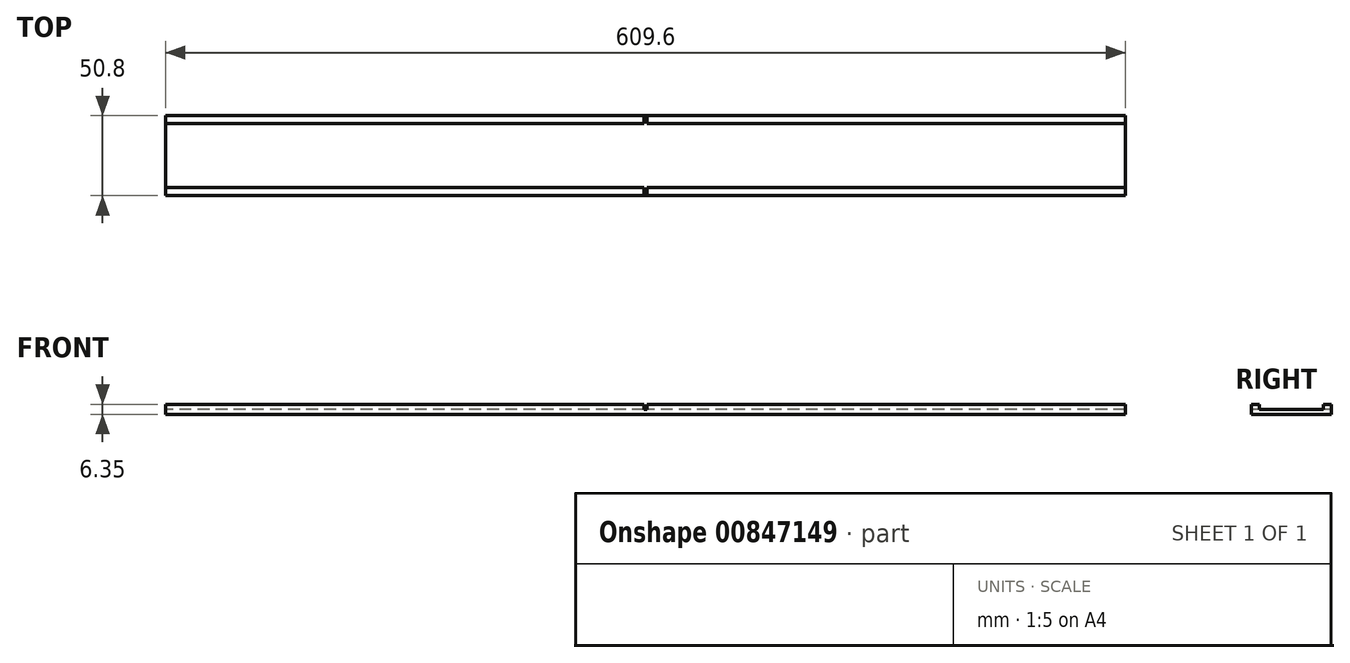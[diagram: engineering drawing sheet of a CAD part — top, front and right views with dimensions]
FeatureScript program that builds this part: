
annotation { "Feature Type Name" : "Feature", "Feature Type Description" : "" }
export const myFeature = defineFeature(function(context is Context, id is Id, definition is map)
    precondition{}
    {
        {
            var Q0;
            Q0=qCreatedBy(makeId("Top.planeOp"),FACE);
            var sketch = newSketch(context, id + "F0", { "sketchPlane" : qUnion([Q0])});
            skLineSegment(sketch, "E0.bottom", {"start": v(304.8, -25.4) * mm, "end": v(-304.8, -25.4) * mm});
            skLineSegment(sketch, "E0.top", {"start": v(304.8, 25.4) * mm, "end": v(-304.8, 25.4) * mm});
            skLineSegment(sketch, "E0.left", {"start": v(304.8, -25.4) * mm, "end": v(304.8, 25.4) * mm});
            skLineSegment(sketch, "E0.right", {"start": v(-304.8, -25.4) * mm, "end": v(-304.8, 25.4) * mm});
            skPoint(sketch, "E0.middle", {"position": v(0, 0) * mm});
            skSolve(sketch);
        }
        {
            var Q0;
            Q0 = qSketchRegion(id + "F0", true);
            extrude(context, id + "F1", {"entities" : qUnion([Q0]), "depth" : 6.35 * mm, "offsetDistance" : 25.4 * mm});
        }
        {
            var Q0;
            Q0=makeQuery(id+"F1.opExtrude","CAP_FACE",FACE,{"disambiguationData":[OSD([sQuery(id+"F0.wireOp",EDGE,"E0.bottom"),sQuery(id+"F0.wireOp",EDGE,"E0.top"),sQuery(id+"F0.wireOp",EDGE,"E0.left"),sQuery(id+"F0.wireOp",EDGE,"E0.right")])],"isStart":false});
            var sketch = newSketch(context, id + "F2", { "sketchPlane" : qUnion([Q0])});
            skLineSegment(sketch, "E1.bottom", {"start": v(304.8, -20.32) * mm, "end": v(-304.8, -20.32) * mm});
            skLineSegment(sketch, "E1.top", {"start": v(304.8, 20.32) * mm, "end": v(-304.8, 20.32) * mm});
            skLineSegment(sketch, "E1.left", {"start": v(304.8, -20.32) * mm, "end": v(304.8, 20.32) * mm});
            skLineSegment(sketch, "E1.right", {"start": v(-304.8, -20.32) * mm, "end": v(-304.8, 20.32) * mm});
            skPoint(sketch, "E1.middle", {"position": v(0, 0) * mm});
            skSolve(sketch);
        }
        {
            var Q0;
            Q0 = qSketchRegion(id + "F2", true);
            extrude(context, id + "F3", {"entities" : qUnion([Q0]), "operationType" : NewBodyOperationType.REMOVE, "oppositeDirection" : true, "depth" : 3.17 * mm, "offsetDistance" : 25.4 * mm});
        }
        {
            var Q0;
            Q0=makeQuery(id+"F1.opExtrude","SWEPT_FACE",FACE,{"disambiguationData":[OSD([sQuery(id+"F0.wireOp",EDGE,"E0.bottom")])]});
            var sketch = newSketch(context, id + "F4", { "sketchPlane" : qUnion([Q0])});
            skPoint(sketch, "E2.endSnap0", {"position": v(0, 0) * mm});
            skLineSegment(sketch, "E3.bottom", {"start": v(1.02, 3.18) * mm, "end": v(-1.02, 3.18) * mm});
            skLineSegment(sketch, "E3.top", {"start": v(1.02, 6.35) * mm, "end": v(-1.02, 6.35) * mm});
            skLineSegment(sketch, "E3.left", {"start": v(1.02, 3.18) * mm, "end": v(1.02, 6.35) * mm});
            skLineSegment(sketch, "E3.right", {"start": v(-1.02, 3.18) * mm, "end": v(-1.02, 6.35) * mm});
            skPoint(sketch, "E3.middle", {"position": v(0, 4.76) * mm});
            skSolve(sketch);
        }
        {
            var Q0;
            Q0 = qSketchRegion(id + "F4", true);
            var Q1;
            Q1=makeQuery(id+"F1.opExtrude","SWEPT_FACE",FACE,{"disambiguationData":[OSD([sQuery(id+"F0.wireOp",EDGE,"E0.top")])]});
            extrude(context, id + "F5", {"entities" : qUnion([Q0]), "operationType" : NewBodyOperationType.REMOVE, "endBound" : BoundingType.UP_TO_SURFACE, "oppositeDirection" : true, "depth" : 25.4 * mm, "endBoundEntityFace" : qUnion([Q1]), "offsetDistance" : 25.4 * mm});
        }
    });
